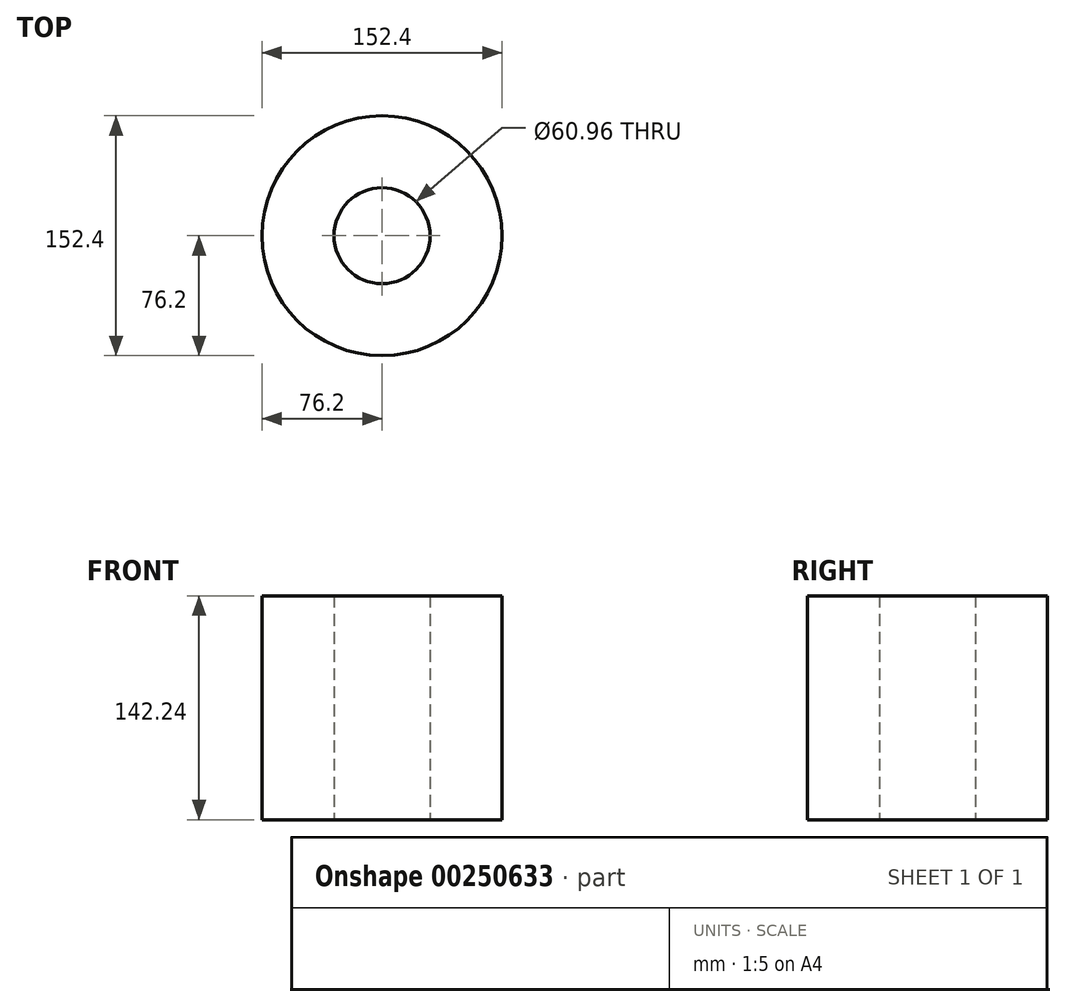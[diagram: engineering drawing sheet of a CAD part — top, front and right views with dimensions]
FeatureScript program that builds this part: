
annotation { "Feature Type Name" : "Feature", "Feature Type Description" : "" }
export const myFeature = defineFeature(function(context is Context, id is Id, definition is map)
    precondition{}
    {
        {
            var Q0;
            Q0=qCreatedBy(makeId("Top.planeOp"),FACE);
            var sketch = newSketch(context, id + "F0", { "sketchPlane" : qUnion([Q0])});
            skCircle(sketch, "E0", {"center": v(0, 0) * mm, "radius": 76.2 * mm});
            skCircle(sketch, "E1", {"center": v(0, 0) * mm, "radius": 30.48 * mm});
            skSolve(sketch);
        }
        {
            var Q0;
            Q0=makeQuery(id+"F0.imprint","IMPRINT",FACE,{"disambiguationData":[TD([[makeQuery(id+"F0.imprint","IMPRINT",EDGE,{"derivedFrom":sQuery(id+"F0.wireOp",EDGE,"E0")}),1.0]])]});
            extrude(context, id + "F1", {"entities" : qUnion([Q0]), "depth" : 142.24 * mm});
        }
    });
